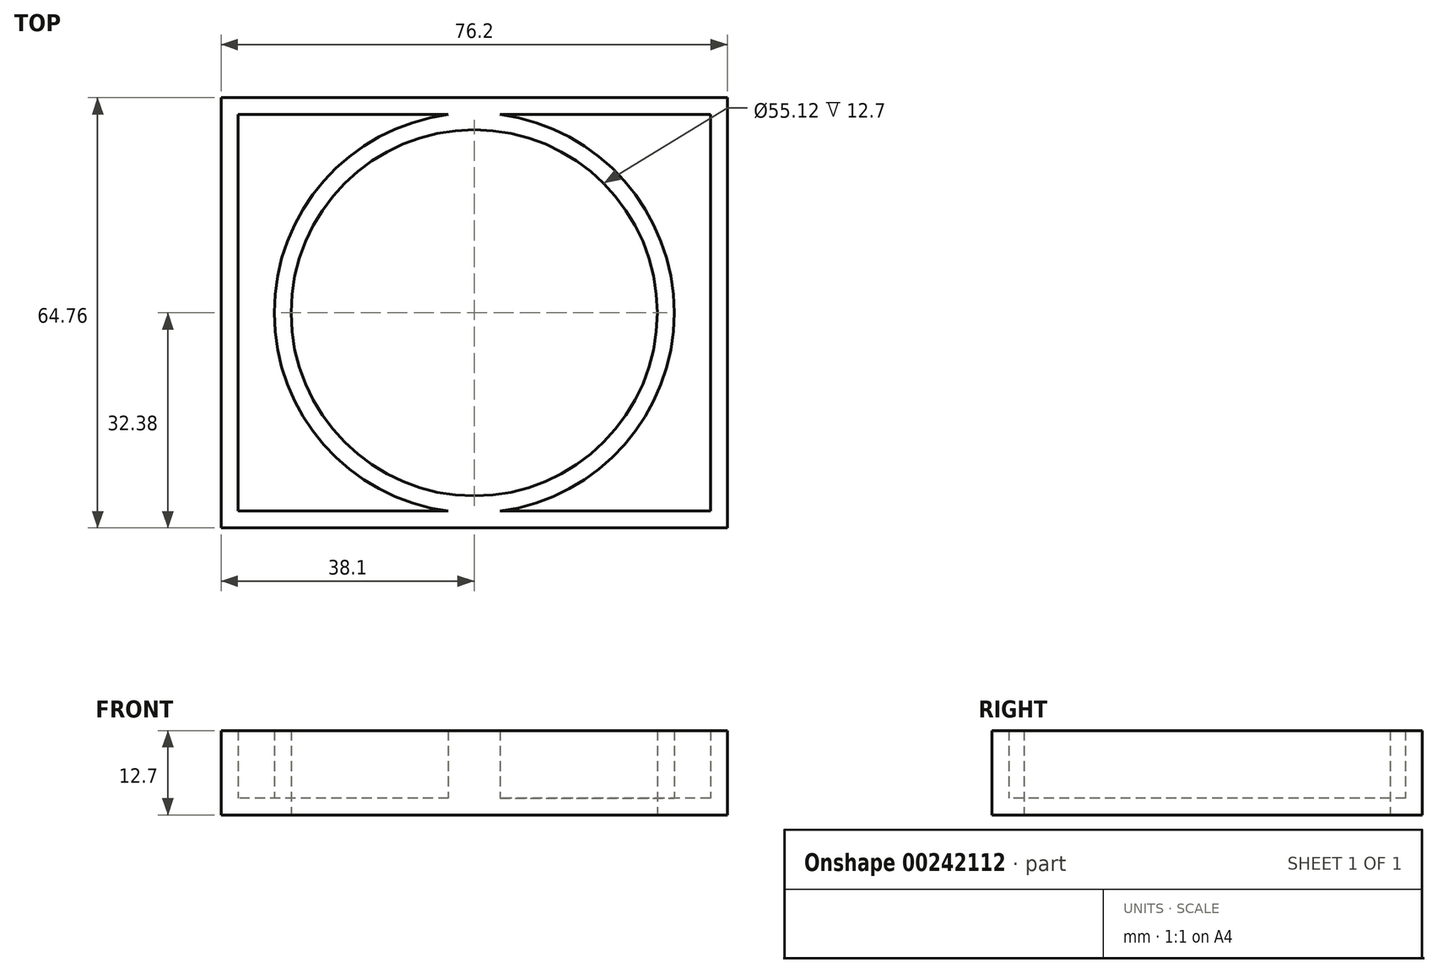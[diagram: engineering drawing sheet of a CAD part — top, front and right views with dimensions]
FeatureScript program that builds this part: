
annotation { "Feature Type Name" : "Feature", "Feature Type Description" : "" }
export const myFeature = defineFeature(function(context is Context, id is Id, definition is map)
    precondition{}
    {
        {
            var Q0;
            Q0=qCreatedBy(makeId("Top.planeOp"),FACE);
            var sketch = newSketch(context, id + "F0", { "sketchPlane" : qUnion([Q0])});
            skCircle(sketch, "E0", {"center": v(0, 0) * mm, "radius": 27.56 * mm});
            skLineSegment(sketch, "E1.bottom", {"start": v(38.1, 32.39) * mm, "end": v(-38.1, 32.39) * mm});
            skLineSegment(sketch, "E1.top", {"start": v(38.1, -32.39) * mm, "end": v(-38.1, -32.39) * mm});
            skLineSegment(sketch, "E1.left", {"start": v(38.1, 32.39) * mm, "end": v(38.1, -32.39) * mm});
            skLineSegment(sketch, "E1.right", {"start": v(-38.1, 32.39) * mm, "end": v(-38.1, -32.39) * mm});
            skSolve(sketch);
        }
        {
            var Q0;
            Q0=makeQuery(id+"F0.imprint","IMPRINT",FACE,{"disambiguationData":[TD([[makeQuery(id+"F0.imprint","IMPRINT",EDGE,{"derivedFrom":sQuery(id+"F0.wireOp",EDGE,"E0")}),-1.0]])]});
            extrude(context, id + "F1", {"entities" : qUnion([Q0]), "depth" : 12.7 * mm});
        }
        {
            var Q0;
            Q0=makeQuery(id+"F1.opExtrude","CAP_FACE",FACE,{"disambiguationData":[OSD([sQuery(id+"F0.wireOp",EDGE,"E0"),sQuery(id+"F0.wireOp",EDGE,"E1.bottom"),sQuery(id+"F0.wireOp",EDGE,"E1.top"),sQuery(id+"F0.wireOp",EDGE,"E1.left"),sQuery(id+"F0.wireOp",EDGE,"E1.right")])],"isStart":false});
            shell(context, id + "F2", {"entities" : qUnion([Q0]), "thickness" : 2.54 * mm});
        }
    });
